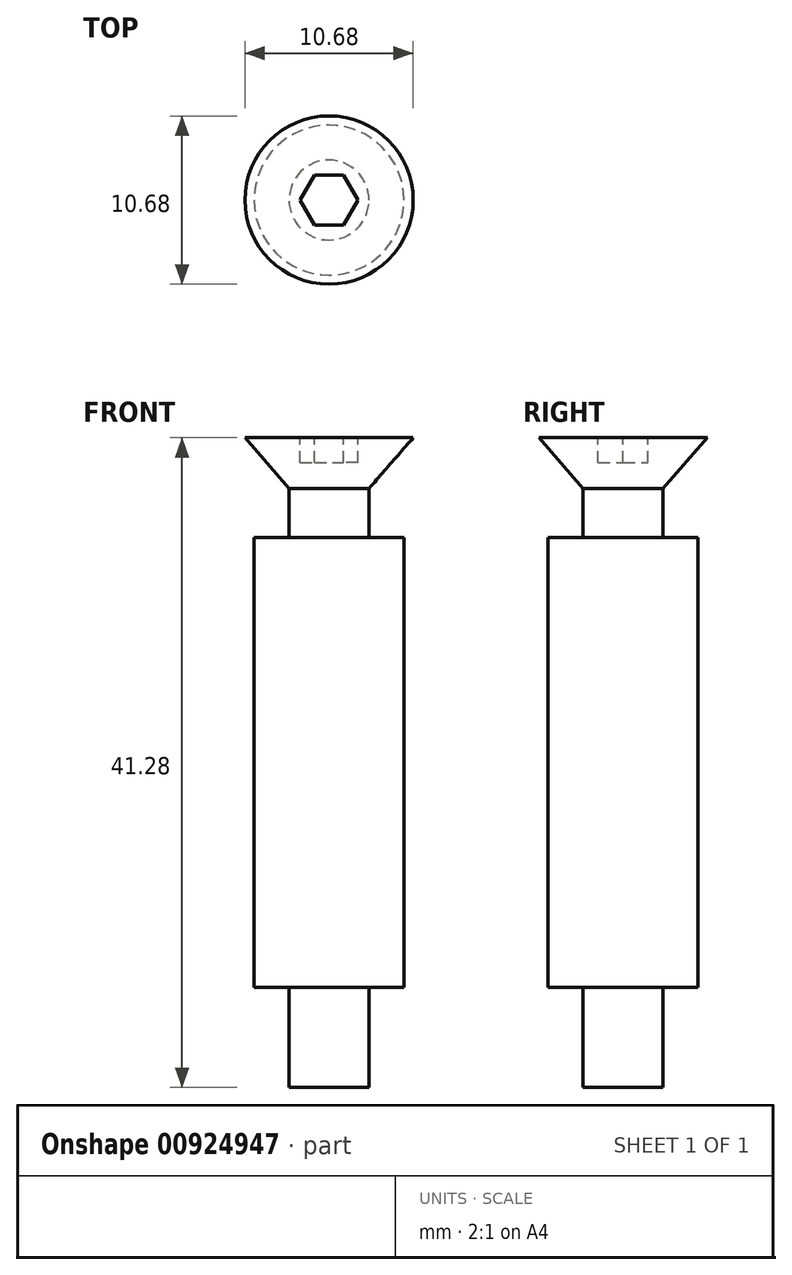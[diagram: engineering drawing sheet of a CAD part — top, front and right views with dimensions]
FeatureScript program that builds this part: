
annotation { "Feature Type Name" : "Feature", "Feature Type Description" : "" }
export const myFeature = defineFeature(function(context is Context, id is Id, definition is map)
    precondition{}
    {
        {
            var Q0;
            Q0=qCreatedBy(makeId("Front.planeOp"),FACE);
            var sketch = newSketch(context, id + "F0", { "sketchPlane" : qUnion([Q0])});
            skLineSegment(sketch, "E0", {"start": v(0, 0) * mm, "end": v(0, -3.23) * mm});
            skLineSegment(sketch, "E1", {"start": v(0, -3.23) * mm, "end": v(2.54, -3.23) * mm, "construction": true});
            skLineSegment(sketch, "E2", {"start": v(2.54, -3.23) * mm, "end": v(5.34, 0) * mm});
            skLineSegment(sketch, "E3", {"start": v(5.34, 0) * mm, "end": v(0, 0) * mm});
            skLineSegment(sketch, "E4", {"start": v(0, -3.23) * mm, "end": v(-2.54, -3.23) * mm, "construction": true});
            skLineSegment(sketch, "E5", {"start": v(-2.54, -3.23) * mm, "end": v(-5.34, 0) * mm, "construction": true});
            skLineSegment(sketch, "E6", {"start": v(-5.34, 0) * mm, "end": v(0, 0) * mm, "construction": true});
            skLineSegment(sketch, "E7", {"start": v(0, -3.23) * mm, "end": v(0, -41.28) * mm});
            skLineSegment(sketch, "E8", {"start": v(0, -41.28) * mm, "end": v(2.54, -41.28) * mm});
            skLineSegment(sketch, "E9", {"start": v(2.54, -41.28) * mm, "end": v(2.54, -3.23) * mm, "construction": true});
            skLineSegment(sketch, "E10", {"start": v(2.54, -3.23) * mm, "end": v(2.54, -6.35) * mm});
            skLineSegment(sketch, "E11", {"start": v(2.54, -6.35) * mm, "end": v(4.76, -6.35) * mm});
            skLineSegment(sketch, "E12", {"start": v(4.76, -6.35) * mm, "end": v(4.76, -34.93) * mm});
            skLineSegment(sketch, "E13", {"start": v(4.76, -34.93) * mm, "end": v(2.54, -34.93) * mm});
            skLineSegment(sketch, "E14", {"start": v(2.54, -34.93) * mm, "end": v(2.54, -41.28) * mm});
            skSolve(sketch);
        }
        {
            var Q0;
            Q0 = qSketchRegion(id + "F0", true);
            var Q1;
            Q1 = qConstructionFilter(qBodyType(qCreatedBy(id + "F0" ,EDGE), BodyType.WIRE), ConstructionObject.NO);
            var Q2;
            Q2=sQuery(id+"F0.wireOp",EDGE,"E7");
            revolve(context, id + "F1", {"surfaceOperationType" : NewSurfaceOperationType.NEW, "entities" : qUnion([Q0]), "surfaceEntities" : qUnion([Q1]), "axis" : qUnion([Q2]), "revolveType" : RevolveType.FULL});
        }
        {
            var Q0;
            Q0=makeQuery(id+"F1.opRevolve","SWEPT_FACE",FACE,{"disambiguationData":[OSD([sQuery(id+"F0.wireOp",EDGE,"E3")])]});
            var sketch = newSketch(context, id + "F2", { "sketchPlane" : qUnion([Q0])});
            skCircle(sketch, "E15.cCircle", {"center": v(0, 0) * mm, "radius": 1.59 * mm, "construction": true});
            skLineSegment(sketch, "E15.0", {"start": v(-0.92, 1.59) * mm, "end": v(0.92, 1.59) * mm});
            skLineSegment(sketch, "E15.1", {"start": v(0.92, 1.59) * mm, "end": v(1.83, 0) * mm});
            skLineSegment(sketch, "E15.2", {"start": v(1.83, 0) * mm, "end": v(0.92, -1.59) * mm});
            skLineSegment(sketch, "E15.3", {"start": v(0.92, -1.59) * mm, "end": v(-0.92, -1.59) * mm});
            skLineSegment(sketch, "E15.4", {"start": v(-0.92, -1.59) * mm, "end": v(-1.83, 0) * mm});
            skLineSegment(sketch, "E15.5", {"start": v(-1.83, 0) * mm, "end": v(-0.92, 1.59) * mm});
            skPoint(sketch, "E15.0.midPoint", {"position": v(0, 1.59) * mm});
            skSolve(sketch);
        }
        {
            var Q0;
            Q0 = qSketchRegion(id + "F2", true);
            extrude(context, id + "F3", {"entities" : qUnion([Q0]), "operationType" : NewBodyOperationType.REMOVE, "oppositeDirection" : true, "depth" : 1.59 * mm, "offsetDistance" : 25.4 * mm});
        }
    });
